# Revit family: ПИК ЭНЕРГО UKE Лючок простой, cерия BS, с выводом для кабеля UKE125 V
name_source: partatom
category: Соединительные детали кабельных лотков
revit_build: Autodesk Revit 2015 (Build: 20141119_1515(x64)
units: mm (PartAtom-declared; Revit-internal decimal feet)

## types (3) — shared parameters
Отметка по умолчанию = 1219 мм
Рзм.B = 125 мм
Рзм.L = 125 мм
Рзм.eb = 78 мм
Рзм.el = 116 мм
Рзм.t = 2 мм
Спец.URLСсылкаСоединителяЛоткаКабельногоКанала = http://www.pik-energo.ru
Спец.ЕдИзмСоединителяЛоткаКабельногоКанала = шт.
Спец.ИзготовительСоединителяЛоткаКабельногоКанала = ПИК-ЭНЕРГО
Спец.НаименованиеИТенхХарСоединителяЛоткаКабельногоКанала = Лючок простой, cерия BS, с выводом для кабеля

## per-type parameters (varying)
| type | Пр.НаименованиеСоединителяЛоткаКабельногоКанала | Рзм.H | Рзм.Hmax | Рзм.Hmin | Рзм.T | Спец.КодОборудИзделияМатериалаСоединителяЛоткаКабельногоКанала | Спец.МассаТекстСоединителяЛоткаКабельногоКанала |
| UKE125 15-V E | Лючок простой четырёхугольный, из нержавеющей стали для монтажа двух модулей 45x45 мм и
двух слаботочных модулей | 15 мм | 125 мм | 90 мм | 12 мм | UKE125 15-V E | 1.74 |
| UKE125 25-V E | Лючок простой четырёхугольный, из нержавеющей стали для монтажа двух модулей 45x45 мм и
двух слаботочных модулей | 25 мм | 135 мм | 100 мм | 22 мм | UKE125 15-V E | 1.93 |
| UKE125 25-V MS | Лючок простой четырёхугольный, из латуни для монтажа двух модулей 45x45 мм и
двух слаботочных модулей | 25 мм | 135 мм | 100 мм | 22 мм | UKE125 25-V MS | 1.74 |

## geometry (parser evidence)
native form markers: Blend x2
no freeform markers — native parametric forms only
